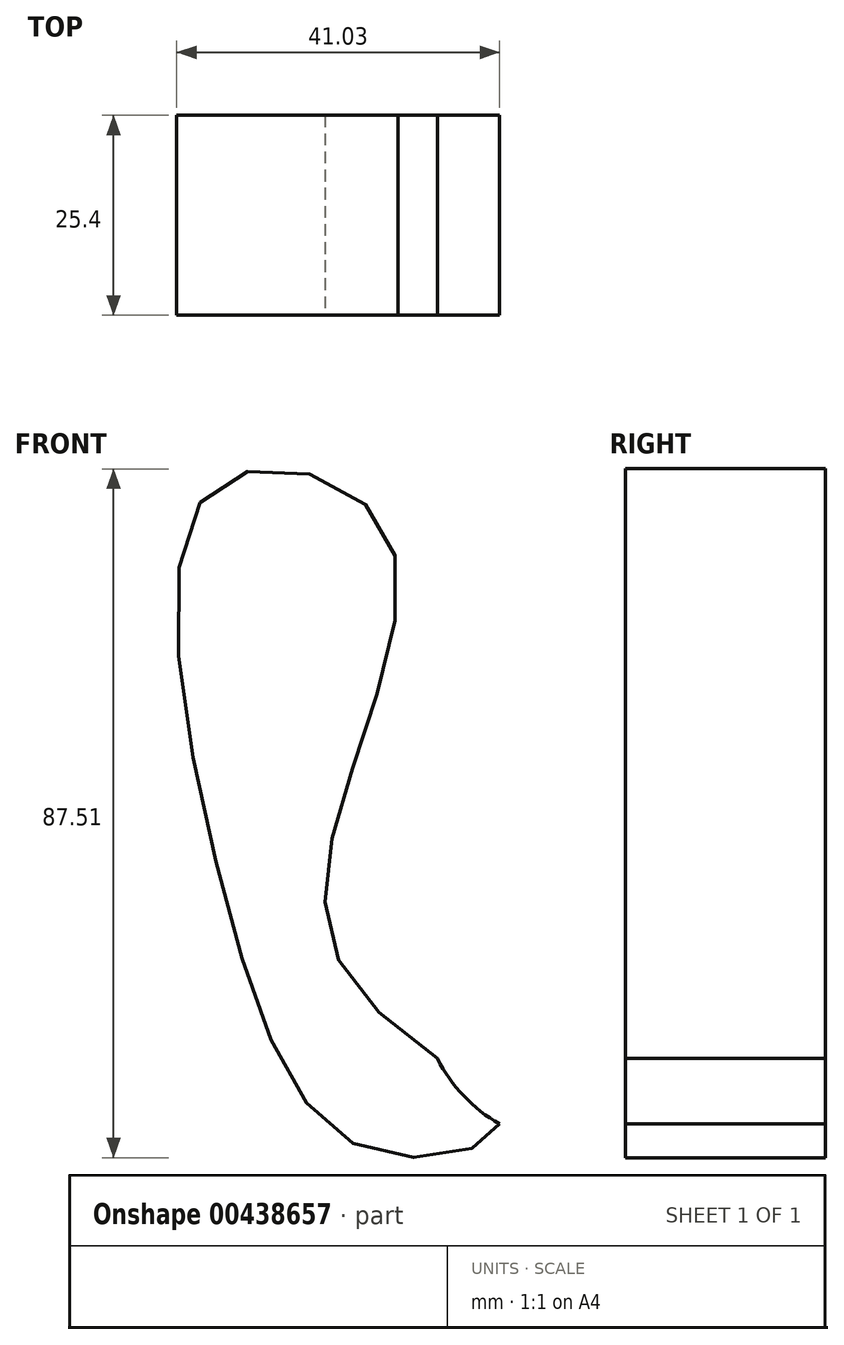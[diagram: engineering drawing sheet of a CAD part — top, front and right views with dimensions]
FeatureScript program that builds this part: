
annotation { "Feature Type Name" : "Feature", "Feature Type Description" : "" }
export const myFeature = defineFeature(function(context is Context, id is Id, definition is map)
    precondition{}
    {
        {
            var Q0;
            Q0=qCreatedBy(makeId("Front.planeOp"),FACE);
            var sketch = newSketch(context, id + "F0", { "sketchPlane" : qUnion([Q0])});
            skCircle(sketch, "E0", {"center": v(0, 0) * mm, "radius": 20.09 * mm});
            skFitSpline(sketch, "E1", {"points": [v(-10, -17.42) * mm, v(-26.13, -20.9) * mm, v(-44.8, 11.2) * mm, v(-46.3, 63.46) * mm, v(-25.01, 58.98) * mm, v(-29.12, 26.5) * mm, v(-28.37, 0) * mm, v(-10, -17.42) * mm]});
            skSolve(sketch);
        }
        {
            var Q0;
            {var subQ0=sQuery(id+"F0.wireOp",EDGE,"E1");var subQ1=sQuery(id+"F0.wireOp",EDGE,"E0");var subQ2=makeQuery(id+"F0.imprint","INTERSECT",VERTEX,{"disambiguationData":[OD(0.0)],"derivedFrom":[subQ1,subQ0]});Q0=makeQuery(id+"F0.imprint","IMPRINT",FACE,{"disambiguationData":[TD([[makeQuery(id+"F0.imprint","IMPRINT",EDGE,{"disambiguationData":[TD([[subQ2,-1.0]])],"derivedFrom":subQ1}),-1.0]])]});}
            extrude(context, id + "F1", {"entities" : qUnion([Q0]), "depth" : 25.4 * mm});
        }
    });
